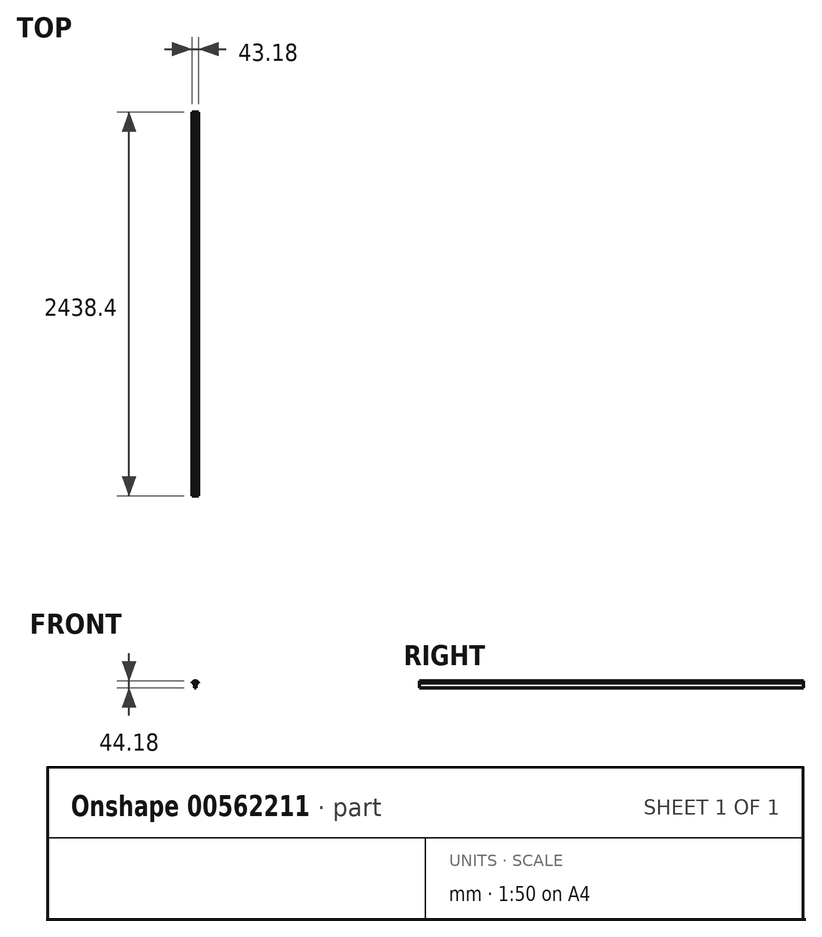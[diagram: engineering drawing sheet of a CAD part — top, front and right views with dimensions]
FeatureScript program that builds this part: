
annotation { "Feature Type Name" : "Feature", "Feature Type Description" : "" }
export const myFeature = defineFeature(function(context is Context, id is Id, definition is map)
    precondition{}
    {
        {
            var Q0;
            Q0=qCreatedBy(makeId("Front.planeOp"),FACE);
            var sketch = newSketch(context, id + "F0", { "sketchPlane" : qUnion([Q0])});
            skLineSegment(sketch, "E0.bottom", {"start": v(-15.8, 0) * mm, "end": v(-27.39, 0) * mm});
            skLineSegment(sketch, "E0.top", {"start": v(-12.7, 44.18) * mm, "end": v(-30.48, 44.18) * mm});
            skLineSegment(sketch, "E0.left", {"start": v(0, 31.75) * mm, "end": v(0, 34.92) * mm});
            skLineSegment(sketch, "E0.right", {"start": v(-43.18, 31.75) * mm, "end": v(-43.18, 34.92) * mm});
            skLineSegment(sketch, "E1.0", {"start": v(-9.4, 31.75) * mm, "end": v(-15.8, 31.75) * mm});
            skLineSegment(sketch, "E2.0", {"start": v(-30.48, 44.18) * mm, "end": v(-30.48, 42.19) * mm});
            skArc(sketch, "E3", {"start": v(-30.48, 42.19) * mm, "mid": v(-36.37, 39.9) * mm, "end": v(-40.26, 34.92) * mm});
            skPoint(sketch, "E4.trimOffspring.end.orphan", {"position": v(-43.18, 44.18) * mm});
            skLineSegment(sketch, "E5.trimOffspring", {"start": v(-40.26, 34.92) * mm, "end": v(-43.18, 34.92) * mm});
            skLineSegment(sketch, "E6.0", {"start": v(-27.39, 31.75) * mm, "end": v(-27.39, 0) * mm});
            skPoint(sketch, "E7.orphan", {"position": v(-43.18, 0) * mm});
            skLineSegment(sketch, "E8", {"start": v(-33.78, 31.75) * mm, "end": v(-33.78, 32.26) * mm});
            skLineSegment(sketch, "E9", {"start": v(-33.78, 32.26) * mm, "end": v(-43.18, 31.75) * mm});
            skLineSegment(sketch, "E10.MirrorCS", {"start": v(-9.4, 31.75) * mm, "end": v(-9.4, 32.26) * mm});
            skPoint(sketch, "E11.MirrorP", {"position": v(0, 0) * mm});
            skLineSegment(sketch, "E12.MirrorCS", {"start": v(-9.4, 32.26) * mm, "end": v(0, 31.75) * mm});
            skLineSegment(sketch, "E13.MirrorCS", {"start": v(0, 31.75) * mm, "end": v(0, 34.93) * mm});
            skLineSegment(sketch, "E14.MirrorCS", {"start": v(-15.8, 31.75) * mm, "end": v(-15.8, 0) * mm});
            skLineSegment(sketch, "E15.MirrorCS", {"start": v(-2.92, 34.93) * mm, "end": v(0, 34.93) * mm});
            skArc(sketch, "E16.MirrorCS", {"start": v(-12.7, 42.19) * mm, "mid": v(-6.81, 39.9) * mm, "end": v(-2.92, 34.93) * mm});
            skLineSegment(sketch, "E17.MirrorCS", {"start": v(-12.7, 44.18) * mm, "end": v(-12.7, 42.19) * mm});
            skPoint(sketch, "E18.orphan", {"position": v(0, 44.18) * mm});
            skPoint(sketch, "E19.orphan", {"position": v(-27.39, 44.18) * mm});
            skLineSegment(sketch, "E20.trimOffspring", {"start": v(-27.39, 31.75) * mm, "end": v(-33.78, 31.75) * mm});
            skPoint(sketch, "E21.orphan", {"position": v(-15.8, 44.18) * mm});
            skPoint(sketch, "E22.end.orphan", {"position": v(-21.59, 0) * mm});
            skPoint(sketch, "E22.start.orphan", {"position": v(-21.6, 44.18) * mm});
            skSolve(sketch);
        }
        {
            var Q0;
            Q0 = qSketchRegion(id + "F0", true);
            extrude(context, id + "F1", {"entities" : qUnion([Q0]), "depth" : 2438.4 * mm, "offsetDistance" : 25.4 * mm});
        }
    });
